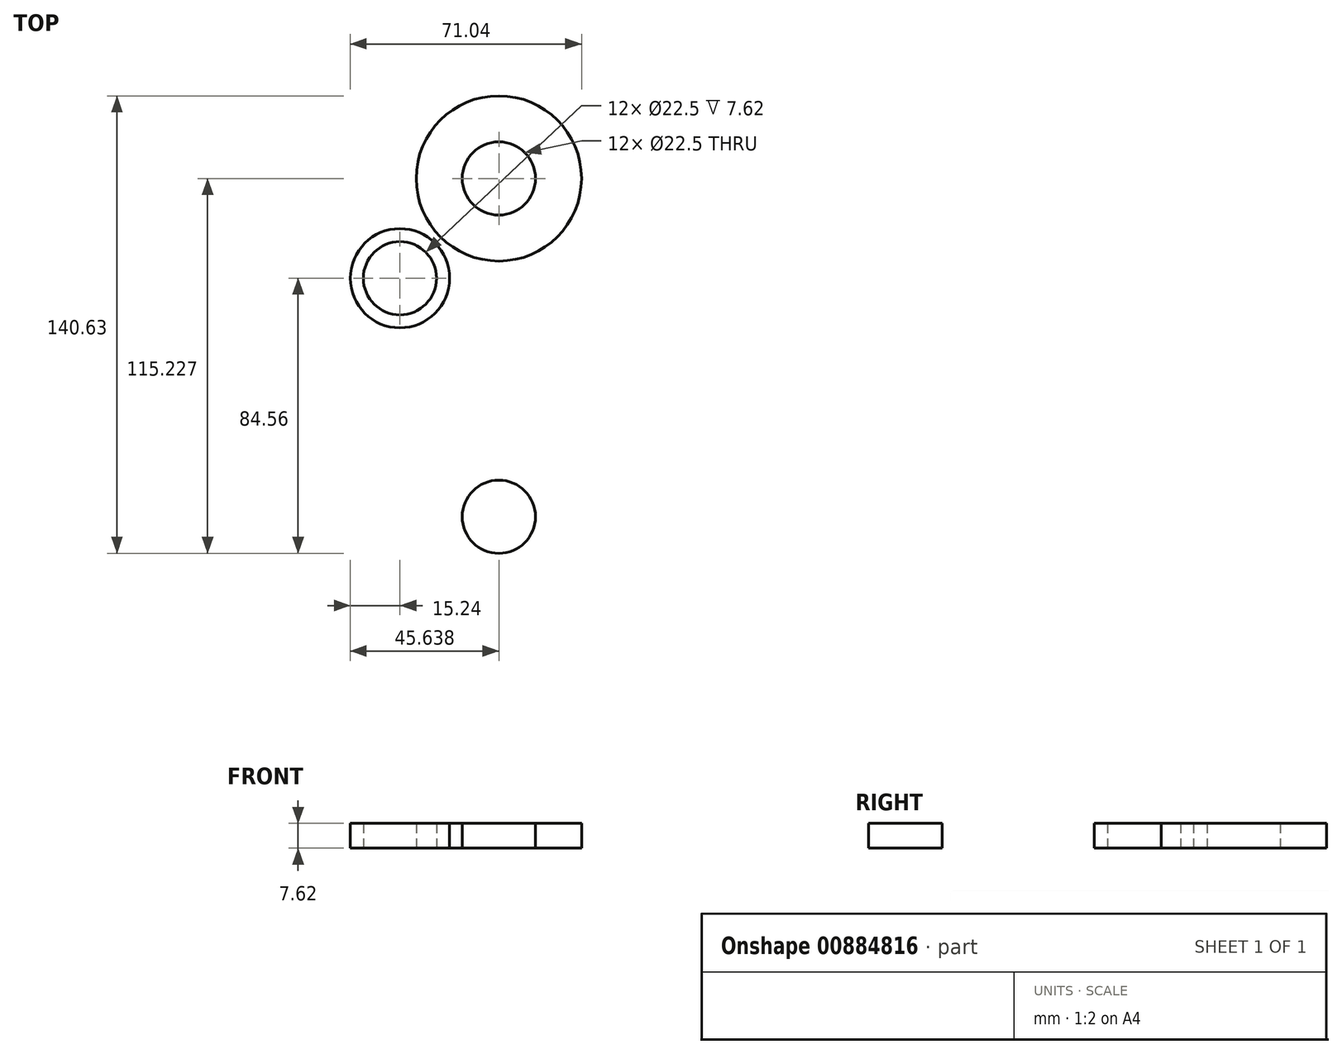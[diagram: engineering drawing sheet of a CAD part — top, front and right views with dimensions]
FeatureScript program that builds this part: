
annotation { "Feature Type Name" : "Feature", "Feature Type Description" : "" }
export const myFeature = defineFeature(function(context is Context, id is Id, definition is map)
    precondition{}
    {
        {
            var Q0;
            Q0=qCreatedBy(makeId("Top.planeOp"),FACE);
            var sketch = newSketch(context, id + "F0", { "sketchPlane" : qUnion([Q0])});
            skCircle(sketch, "E0", {"center": v(0, 0) * mm, "radius": 15.24 * mm});
            skCircle(sketch, "E1", {"center": v(30.4, 30.67) * mm, "radius": 25.4 * mm});
            skCircle(sketch, "E2", {"center": v(0, 0) * mm, "radius": 11.25 * mm});
            skCircle(sketch, "E3", {"center": v(30.4, 30.67) * mm, "radius": 11.25 * mm});
            skLineSegment(sketch, "E4", {"start": v(-32.8, -21.32) * mm, "end": v(75.44, -21.32) * mm});
            skCircle(sketch, "E5.MirrorC", {"center": v(0, -42.64) * mm, "radius": 15.24 * mm});
            skCircle(sketch, "E6.MirrorC", {"center": v(0, -42.64) * mm, "radius": 11.25 * mm});
            skCircle(sketch, "E7.MirrorC", {"center": v(30.4, -73.3) * mm, "radius": 11.25 * mm});
            skCircle(sketch, "E8.MirrorC", {"center": v(30.4, -73.3) * mm, "radius": 25.4 * mm});
            skSolve(sketch);
        }
        {
            var Q0;
            Q0=makeQuery(id+"F0.imprint","IMPRINT",FACE,{"disambiguationData":[TD([[makeQuery(id+"F0.imprint","IMPRINT",EDGE,{"derivedFrom":sQuery(id+"F0.wireOp",EDGE,"E0")}),1.0]])]});
            var Q1;
            Q1=makeQuery(id+"F0.imprint","IMPRINT",FACE,{"disambiguationData":[TD([[makeQuery(id+"F0.imprint","IMPRINT",EDGE,{"derivedFrom":sQuery(id+"F0.wireOp",EDGE,"E1")}),1.0]])]});
            var Q2;
            Q2=makeQuery(id+"F0.imprint","IMPRINT",FACE,{"disambiguationData":[TD([[makeQuery(id+"F0.imprint","IMPRINT",EDGE,{"derivedFrom":sQuery(id+"F0.wireOp",EDGE,"E5.MirrorC")}),-1.0]])]});
            var Q3;
            Q3=makeQuery(id+"F0.imprint","IMPRINT",FACE,{"disambiguationData":[TD([[makeQuery(id+"F0.imprint","IMPRINT",EDGE,{"derivedFrom":sQuery(id+"F0.wireOp",EDGE,"E7.MirrorC")}),1.0]])]});
            extrude(context, id + "F1", {"entities" : qUnion([Q0, Q1, Q2, Q3]), "depth" : 7.62 * mm, "offsetDistance" : 25.4 * mm});
        }
    });
